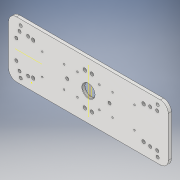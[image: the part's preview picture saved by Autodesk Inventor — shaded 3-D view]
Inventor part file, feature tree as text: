
AUTODESK INVENTOR PART (.ipt)
format: ipt  version: 2019 (Build 230136000, 136)  size: 1,350,144 bytes
history: native  units: mm
features: sketch x10, extrude x9, plane x4, mirror x1, fillet x1
ambient origin geometry x8: Origin, YZ Plane, XZ Plane, XY Plane, X Axis, Y Axis, Z Axis, Center Point
bodies: Solid1 (feature_tree)
feature tree (25):
  extrude  "Extrusion1"  Depth=72.0mm
  extrude  "Extrusion3"  Depth=4.0mm TaperAngle=0.0deg
  extrude  "Extrusion4"  Depth=4.0mm
  plane  "Work Plane1"
  plane  "Work Plane2"
  plane  "Work Plane3"
  sketch  "Sketch7"  dims[d11=6.0mm d12=0.0mm d15=25.0mm]
  extrude  "Extrusion6"  Depth=25.0mm
  extrude  "Extrusion7"  Depth=4.0mm
  plane  "Work Plane4"
  mirror  "Mirror2"
  extrude  "Extrusion8"  Depth=60.0mm TaperAngle=0.0deg
  extrude  "Extrusion9"  [1 undecoded]
  fillet  "Fillet1"  [1 undecoded]
  extrude  "Extrusion10"  Depth=14.0mm
  extrude  "Extrusion11"  Depth=23.0mm
  sketch  "Sketch1"  dims[d0=204.0mm d1=72.0mm]
  sketch  "Sketch3"  dims[d2=10.0mm d3=4.0mm d4=0.0mm]
  sketch  "Sketch4"  dims[d6=4.0mm d10=4.0mm]
  sketch  "Sketch8"  dims[d16=12.5mm d17=4.0mm]
  sketch  "Sketch9"  dims[d19=4.0mm d21=60.0mm d22=0.0mm]
  sketch  "Sketch10"  dims[d23=-100.0mm d24=-36.0mm d36=-36.0mm]
  sketch  "Sketch11"  dims[d37=23.0mm d38=14.0mm]
  sketch  "Sketch12"  dims[d39=14.0mm d40=23.0mm]
  sketch  "Sketch13"  dims[d41=25.0mm d42=14.0mm d43=25.0mm d44=14.0mm d45=4.0mm d46=7.0mm d47=15.5mm d48=4.0mm d49=7.0mm d50=15.5mm d51=4.0mm d52=7.0mm d53=13.5mm d54=10.0mm d55=0.0mm d56=16.0mm d57=2.0mm d58=2.0mm d59=28.0mm d60=28.0mm d61=28.0mm d62=28.0mm d63=22.0mm d64=4.45mm d65=66.1mm d66=4.45mm d67=42.0mm d68=42.0mm d69=66.1mm d70=15.0mm d71=15.0mm d73=22.0mm d74=10.0mm d75=0.0mm d76=-102.0mm d77=4.0mm d78=14.0mm d79=14.0mm d80=10.0mm d81=0.0mm d82=2.2mm d83=2.2mm d84=2.2mm d85=28.0mm d86=28.0mm d87=28.0mm d88=28.0mm d89=14.0mm d90=14.0mm d91=14.0mm d92=14.0mm d93=10.0mm d94=0.0mm d95=0.5mm d96=4.0mm d97=4.0mm d98=75.0mm d99=75.0mm d100=10.0mm d101=0.0mm d102=3.0mm d103=270.0deg d104=3.0mm d105=1.0mm d106=0.0mm]
note: 2 required parameter values undecoded (feature->parameter linkage not recoverable at this tier; creation-order binding heuristic only, values carry confidence <= 0.55)
